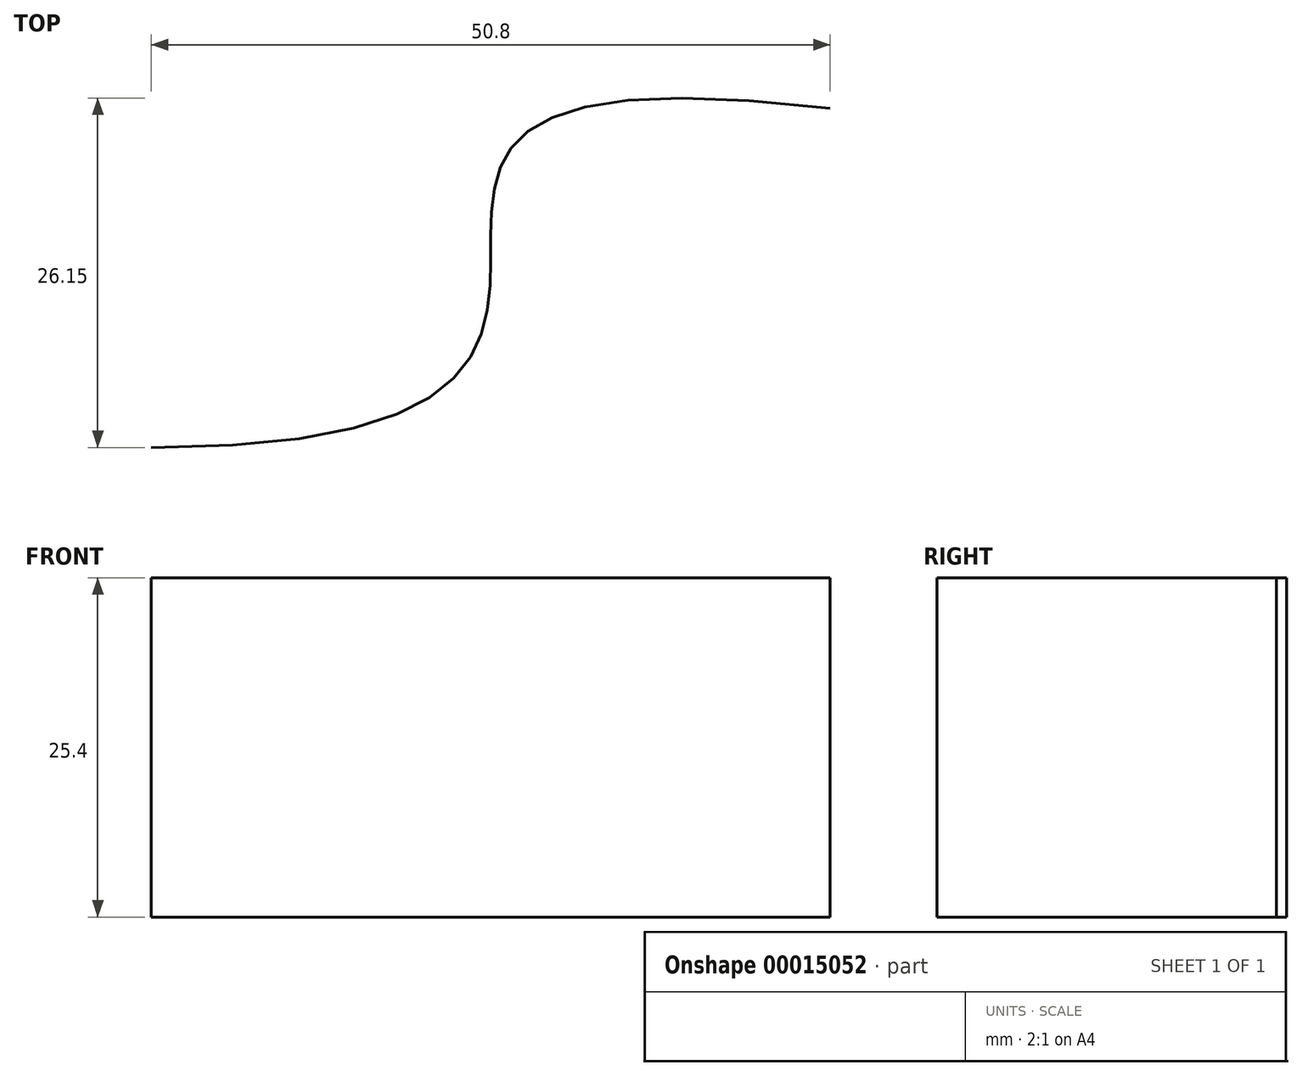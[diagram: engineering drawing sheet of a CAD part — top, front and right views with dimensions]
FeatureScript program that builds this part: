
annotation { "Feature Type Name" : "Feature", "Feature Type Description" : "" }
export const myFeature = defineFeature(function(context is Context, id is Id, definition is map)
    precondition{}
    {
        {
            var Q0;
            Q0=qCreatedBy(makeId("Top.planeOp"),FACE);
            var sketch = newSketch(context, id + "F0", { "sketchPlane" : qUnion([Q0])});
            skFitSpline(sketch, "E0", {"points": [v(0, 0) * mm, v(50.8, 25.4) * mm], "startDerivative": vector(152.4, 0) * mm, "endDerivative": vector(152.4, -17.84) * mm});
            skLineSegment(sketch, "E1", {"start": v(0, 31.35) * mm, "end": v(50.8, 0) * mm, "construction": true});
            skLineSegment(sketch, "E2", {"start": v(0, 31.35) * mm, "end": v(50.8, 25.4) * mm, "construction": true});
            skFitSpline(sketch, "E3", {"points": [v(0, 0) * mm, v(-4, 28.9) * mm], "startDerivative": vector(-44.13, 0) * mm, "endDerivative": vector(19.68, 8.37) * mm});
            skSolve(sketch);
        }
        {
            var Q0;
            Q0 = qSketchRegion(id + "F0", true);
            var Q1;
            Q1=sQuery(id+"F0.wireOp",EDGE,"E0");
            extrude(context, id + "F1", {"entities" : qUnion([Q0]), "bodyType" : ToolBodyType.SURFACE, "surfaceEntities" : qUnion([Q1]), "depth" : 25.4 * mm});
        }
    });
